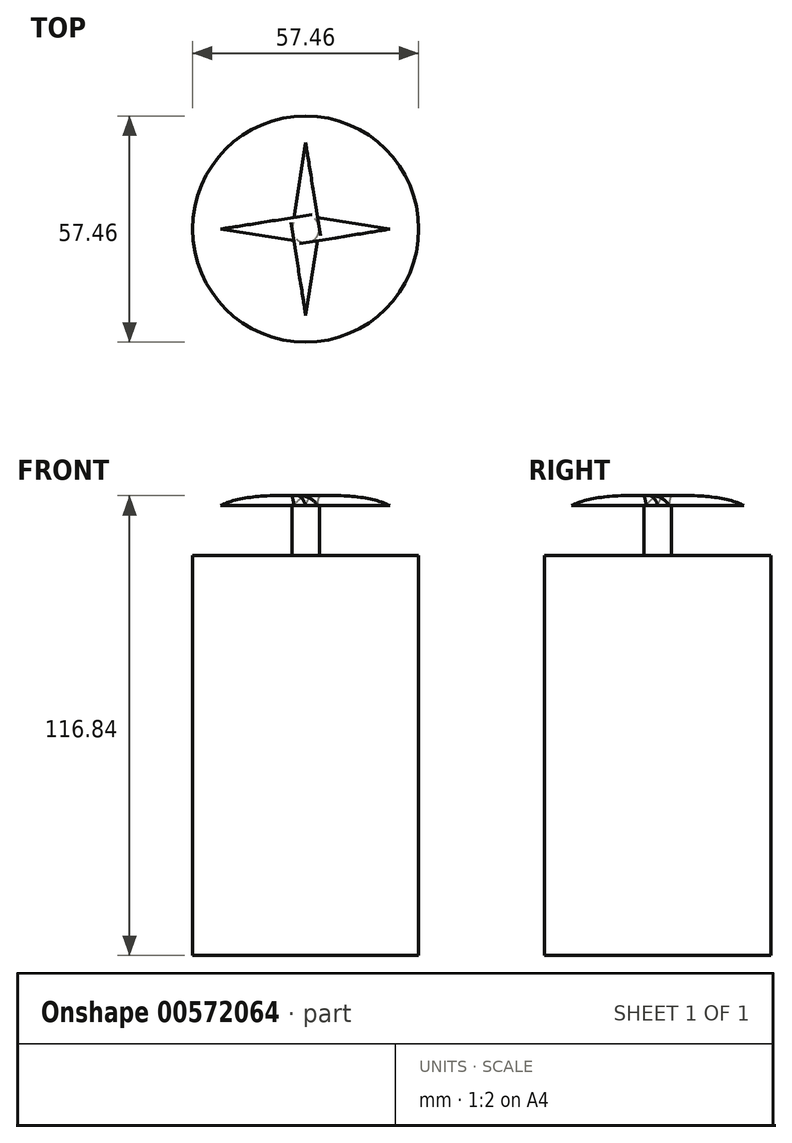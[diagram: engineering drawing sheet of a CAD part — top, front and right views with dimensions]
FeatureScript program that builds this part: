
annotation { "Feature Type Name" : "Feature", "Feature Type Description" : "" }
export const myFeature = defineFeature(function(context is Context, id is Id, definition is map)
    precondition{}
    {
        {
            var Q0;
            Q0=qCreatedBy(makeId("Top.planeOp"),FACE);
            var sketch = newSketch(context, id + "F0", { "sketchPlane" : qUnion([Q0])});
            skCircle(sketch, "E0", {"center": v(0, 0) * mm, "radius": 28.73 * mm});
            skSolve(sketch);
        }
        {
            var Q0;
            Q0=makeQuery(id+"F0.imprint","IMPRINT",FACE,{"disambiguationData":[TD([[makeQuery(id+"F0.imprint","IMPRINT",EDGE,{"derivedFrom":sQuery(id+"F0.wireOp",EDGE,"E0")}),1.0]])]});
            extrude(context, id + "F1", {"entities" : qUnion([Q0]), "depth" : 101.6 * mm, "offsetDistance" : 25.4 * mm});
        }
        {
            var Q0;
            Q0=makeQuery(id+"F1.opExtrude","CAP_FACE",FACE,{"disambiguationData":[OSD([sQuery(id+"F0.wireOp",EDGE,"E0")])],"isStart":false});
            var sketch = newSketch(context, id + "F2", { "sketchPlane" : qUnion([Q0])});
            skCircle(sketch, "E1", {"center": v(0, 0) * mm, "radius": 3.46 * mm});
            skSolve(sketch);
        }
        {
            var Q0;
            Q0 = qSketchRegion(id + "F2", true);
            extrude(context, id + "F3", {"entities" : qUnion([Q0]), "operationType" : NewBodyOperationType.ADD, "depth" : 12.7 * mm, "offsetDistance" : 25.4 * mm});
        }
        {
            var Q0;
            Q0=makeQuery(id+"F3.opExtrude","CAP_FACE",FACE,{"disambiguationData":[OSD([sQuery(id+"F2.wireOp",EDGE,"E1")])],"isStart":false});
            var sketch = newSketch(context, id + "F4", { "sketchPlane" : qUnion([Q0])});
            skLineSegment(sketch, "E2", {"start": v(-3.46, 0) * mm, "end": v(0, 21.92) * mm});
            skLineSegment(sketch, "E3", {"start": v(0, 21.92) * mm, "end": v(3.5, 0) * mm});
            skLineSegment(sketch, "E4", {"start": v(3.5, 0) * mm, "end": v(0, -21.92) * mm});
            skLineSegment(sketch, "E5", {"start": v(0, -21.92) * mm, "end": v(-3.46, 0) * mm});
            skLineSegment(sketch, "E6", {"start": v(0, -3.46) * mm, "end": v(-21.64, 0) * mm});
            skLineSegment(sketch, "E7", {"start": v(-21.64, 0) * mm, "end": v(0, 3.42) * mm});
            skLineSegment(sketch, "E8", {"start": v(0, 3.42) * mm, "end": v(21.37, 0) * mm});
            skLineSegment(sketch, "E9", {"start": v(21.37, 0) * mm, "end": v(0, -3.46) * mm});
            skSolve(sketch);
        }
        {
            var Q0;
            Q0 = qSketchRegion(id + "F4", true);
            extrude(context, id + "F5", {"entities" : qUnion([Q0]), "operationType" : NewBodyOperationType.ADD, "depth" : 2.54 * mm, "offsetDistance" : 25.4 * mm});
        }
        {
            var Q0;
            Q0=makeQuery(id+"F5.opExtrude","CAP_EDGE",EDGE,{"disambiguationData":[OSD([sQuery(id+"F4.wireOp",EDGE,"E4")])],"isStart":false});
            var Q1;
            Q1=makeQuery(id+"F5.opExtrude","CAP_EDGE",EDGE,{"disambiguationData":[OSD([sQuery(id+"F4.wireOp",EDGE,"E8")])],"isStart":false});
            var Q2;
            Q2=makeQuery(id+"F5.opExtrude","CAP_EDGE",EDGE,{"disambiguationData":[OSD([sQuery(id+"F4.wireOp",EDGE,"E2")])],"isStart":false});
            var Q3;
            Q3=makeQuery(id+"F5.opExtrude","CAP_EDGE",EDGE,{"disambiguationData":[OSD([sQuery(id+"F4.wireOp",EDGE,"E6")])],"isStart":false});
            fillet(context, id + "F6", {"entities" : qUnion([Q0, Q1, Q2, Q3]), "radius" : 5.08 * mm, "tangentPropagation" : true, "allowEdgeOverflow" : false});
        }
    });
